# Revit family: PRD_FrankeWS_MxrTps_ExtensionSet_ACET9002
name_source: partatom
category: Specialty Equipment
revit_build: Autodesk Revit 2018 (Build: 20190510_1515(x64)
units: mm (PartAtom-declared; Revit-internal decimal feet)

## family parameters
Always vertical = Yes
Cut with Voids When Loaded = No
OmniClass Number = 23.45.05.14.99
OmniClass Title = Other Sanitary Washing Plumbing Fixtures
Part Type = Normal
Room Calculation Point = No
Round Connector Dimension = Use Diameter
Shared = No
Work Plane-Based = Yes

## types (1)
- ACET9002
    AssetType = Fixed
    BIMObjectName = PRD_AR_MixerTaps_ExtensionSet_ACET9002
    BodyMaterial = PRD_AR_Brass
    Category = Pr_40_20_87_55, Mixer taps
    Default Elevation = 1219 mm
    Description = Extension set for F5E-Therm and F3E-Therm thermostatic mixer DN 15, electronically controlled, for installation in walls, for depth compensation up to 25 mm.
    DurationUnit = year
    Features = for F5E-Therm and F3E-Therm thermostatic mixer DN 15
    GrossWeight = 0.50 kg
    IfcExportAs = IfcSanitaryTerminal
    IfcExportType = USERDEFINED
    Manufacturer = KWC Group AG
    ManufacturerName = KWC Group AG
    ManufacturerURL = www.kwc.com
    Model = ACET9002
    ModelNumber = 2030044782
    ModelReference = ACET9002
    Name = Extension set ACET9002
    NetWeight = 0.45 kg
    NominalDepth = 25 mm  [stored 0.082021 ft]
    NominalLength = 53 mm  [stored 0.173885 ft]
    NominalWidth = 53 mm  [stored 0.173885 ft]
    ProductInformation = https://pim.kwc.com
    Quantity = 1
    QuantityUom = Piece
    Shape = cylinder
    Status = New
    TailorMade = No
    URL = www.kwc.com
    Uniclass2015Code = Pr_40_20_87_55
    Uniclass2015Title = Mixer taps
    Uniclass2015Version = Products v1.17
    Version = 1
    WarrantyDurationUnit = year

note: [stored X ft] marks values corroborated as IEEE doubles in the binary element streams (Revit-internal decimal feet)

## geometry (parser evidence)
native form markers: Sweep x3
no freeform markers — native parametric forms only
